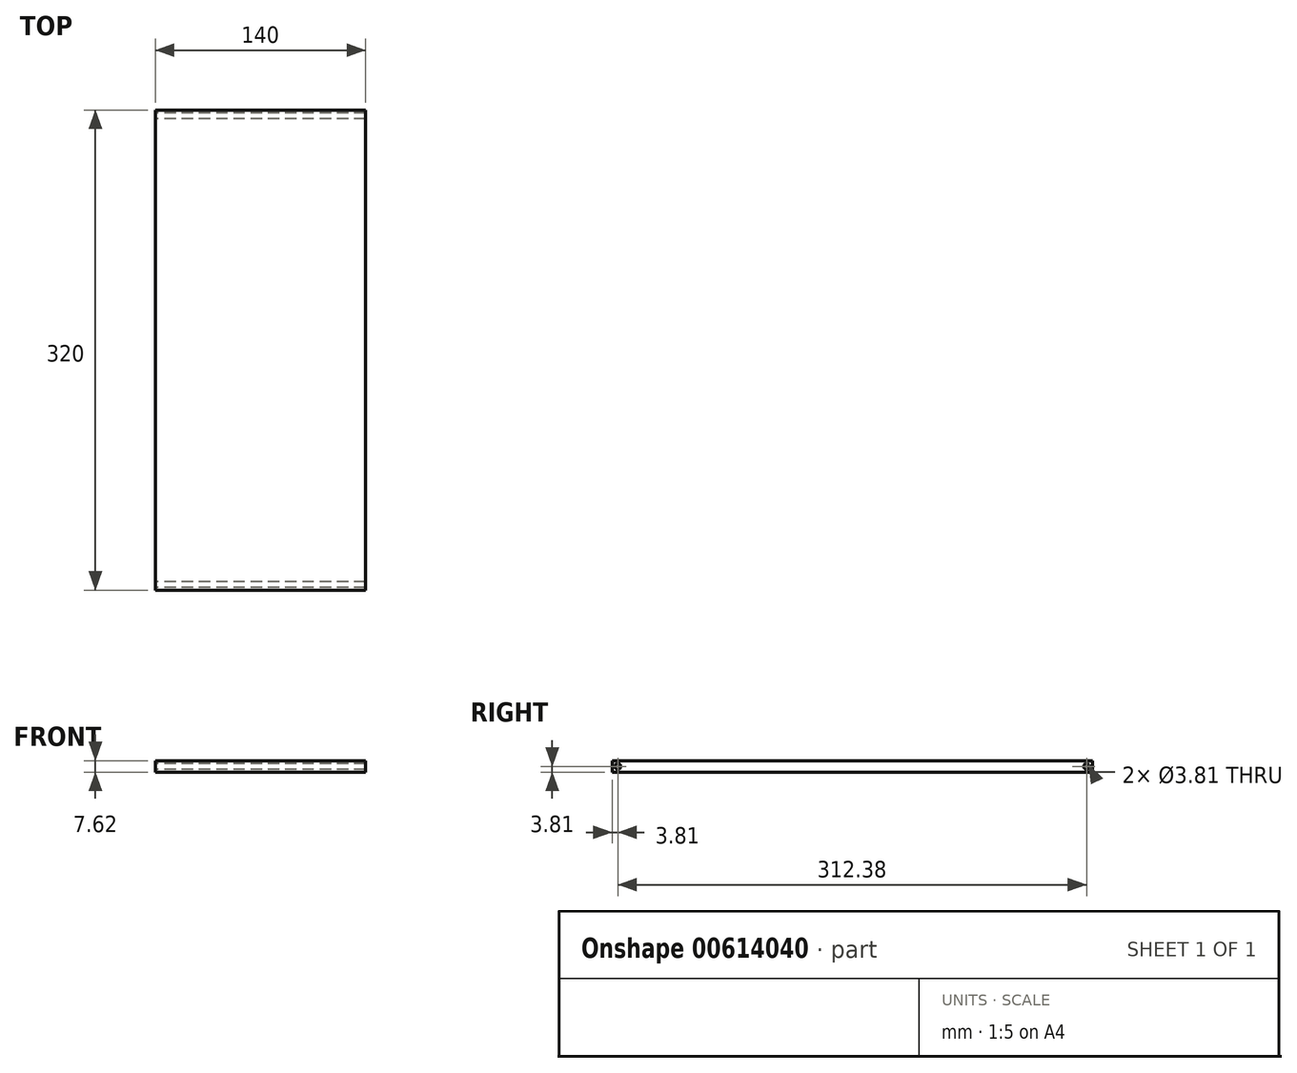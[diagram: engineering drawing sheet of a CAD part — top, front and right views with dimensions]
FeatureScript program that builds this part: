
annotation { "Feature Type Name" : "Feature", "Feature Type Description" : "" }
export const myFeature = defineFeature(function(context is Context, id is Id, definition is map)
    precondition{}
    {
        {
            var Q0;
            Q0=qCreatedBy(makeId("Top.planeOp"),FACE);
            var sketch = newSketch(context, id + "F0", { "sketchPlane" : qUnion([Q0])});
            skLineSegment(sketch, "E0.bottom", {"start": v(-70, 160) * mm, "end": v(70, 160) * mm});
            skLineSegment(sketch, "E0.top", {"start": v(-70, -160) * mm, "end": v(70, -160) * mm});
            skLineSegment(sketch, "E0.left", {"start": v(-70, 160) * mm, "end": v(-70, -160) * mm});
            skLineSegment(sketch, "E0.right", {"start": v(70, 160) * mm, "end": v(70, -160) * mm});
            skPoint(sketch, "E0.middle", {"position": v(0, 0) * mm});
            skSolve(sketch);
        }
        {
            var Q0;
            Q0 = qSketchRegion(id + "F0", true);
            extrude(context, id + "F1", {"entities" : qUnion([Q0]), "depth" : 7.62 * mm, "offsetDistance" : 25.4 * mm});
        }
        {
            var Q0;
            Q0=makeQuery(id+"F1.opExtrude","SWEPT_FACE",FACE,{"disambiguationData":[OSD([sQuery(id+"F0.wireOp",EDGE,"E0.left")])]});
            var sketch = newSketch(context, id + "F2", { "sketchPlane" : qUnion([Q0])});
            skSolve(sketch);
        }
        {
            var Q0;
            {var subQ0=sQuery(id+"F0.wireOp",EDGE,"E0.left");Q0=makeQuery(id+"F2.imprint","IMPRINT",FACE,{"disambiguationData":[TD([[makeQuery(id+"F2.imprint","IMPRINT",EDGE,{"derivedFrom":makeQuery(id+"F1.opExtrude","CAP_EDGE",EDGE,{"disambiguationData":[OSD([subQ0])],"isStart":true})}),1.0]])]});}
            var sketch = newSketch(context, id + "F3", { "sketchPlane" : qUnion([Q0])});
            skCircle(sketch, "E1", {"center": v(156.2, 3.81) * mm, "radius": 1.9 * mm});
            skSolve(sketch);
        }
        {
            var Q0;
            {var subQ0=sQuery(id+"F0.wireOp",EDGE,"E0.left");Q0=makeQuery(id+"F2.imprint","IMPRINT",FACE,{"disambiguationData":[TD([[makeQuery(id+"F2.imprint","IMPRINT",EDGE,{"derivedFrom":makeQuery(id+"F1.opExtrude","CAP_EDGE",EDGE,{"disambiguationData":[OSD([subQ0])],"isStart":true})}),1.0]])]});}
            var sketch = newSketch(context, id + "F4", { "sketchPlane" : qUnion([Q0])});
            skCircle(sketch, "E2", {"center": v(-156.19, 3.81) * mm, "radius": 1.9 * mm});
            skSolve(sketch);
        }
        {
            var Q0;
            Q0 = qSketchRegion(id + "F4", true);
            var Q1;
            Q1=sQuery(id+"F4.wireOp",EDGE,"E2");
            extrude(context, id + "F5", {"entities" : qUnion([Q0]), "operationType" : NewBodyOperationType.REMOVE, "surfaceEntities" : qUnion([Q1]), "oppositeDirection" : true, "depth" : 140 * mm, "offsetDistance" : 25.4 * mm});
        }
        {
            var Q0;
            Q0 = qSketchRegion(id + "F3", true);
            var Q1;
            Q1=sQuery(id+"F3.wireOp",EDGE,"E1");
            extrude(context, id + "F6", {"entities" : qUnion([Q0]), "operationType" : NewBodyOperationType.REMOVE, "surfaceEntities" : qUnion([Q1]), "oppositeDirection" : true, "depth" : 140 * mm, "offsetDistance" : 25.4 * mm});
        }
    });
